# Revit family: TET1UB#CP_TUS
name_source: partatom
category: Plumbing Fixtures
revit_build: Autodesk Revit 2018 (Build: 20170223_1515(x64)
units: mm (PartAtom-declared; Revit-internal decimal feet)

## family parameters
Always vertical = Yes
Cut with Voids When Loaded = No
OmniClass Number = 23.45.00.00
OmniClass Title = Sanitary, Laundry, and Cleaning Equipment
Part Type = Normal
Room Calculation Point = No
Round Connector Dimension = Use Diameter
Shared = No
Work Plane-Based = No

## types (1)
- TET1UB#CP_TUS
    CW Connection = Yes
    Description = Toilet sensor Flush Valve
    Drain Included = No
    Finish = <By Category>
    Flow rate = 3.8LPF
    HW Connection = No
    Height = 205.5 mm
    Length = 90.5 mm
    Manufacturer = TOTO LTD.
    Material = Zinc die casting
    Model = TET1UB#CP
    URL = https://www.totousa.com
    Vent Connection = No
    Waste Connection = No
    Water Pressure = 35psi-125psi
    Width = 117.4 mm

## geometry (parser evidence)
native form markers: Sweep x2
no freeform markers — native parametric forms only
